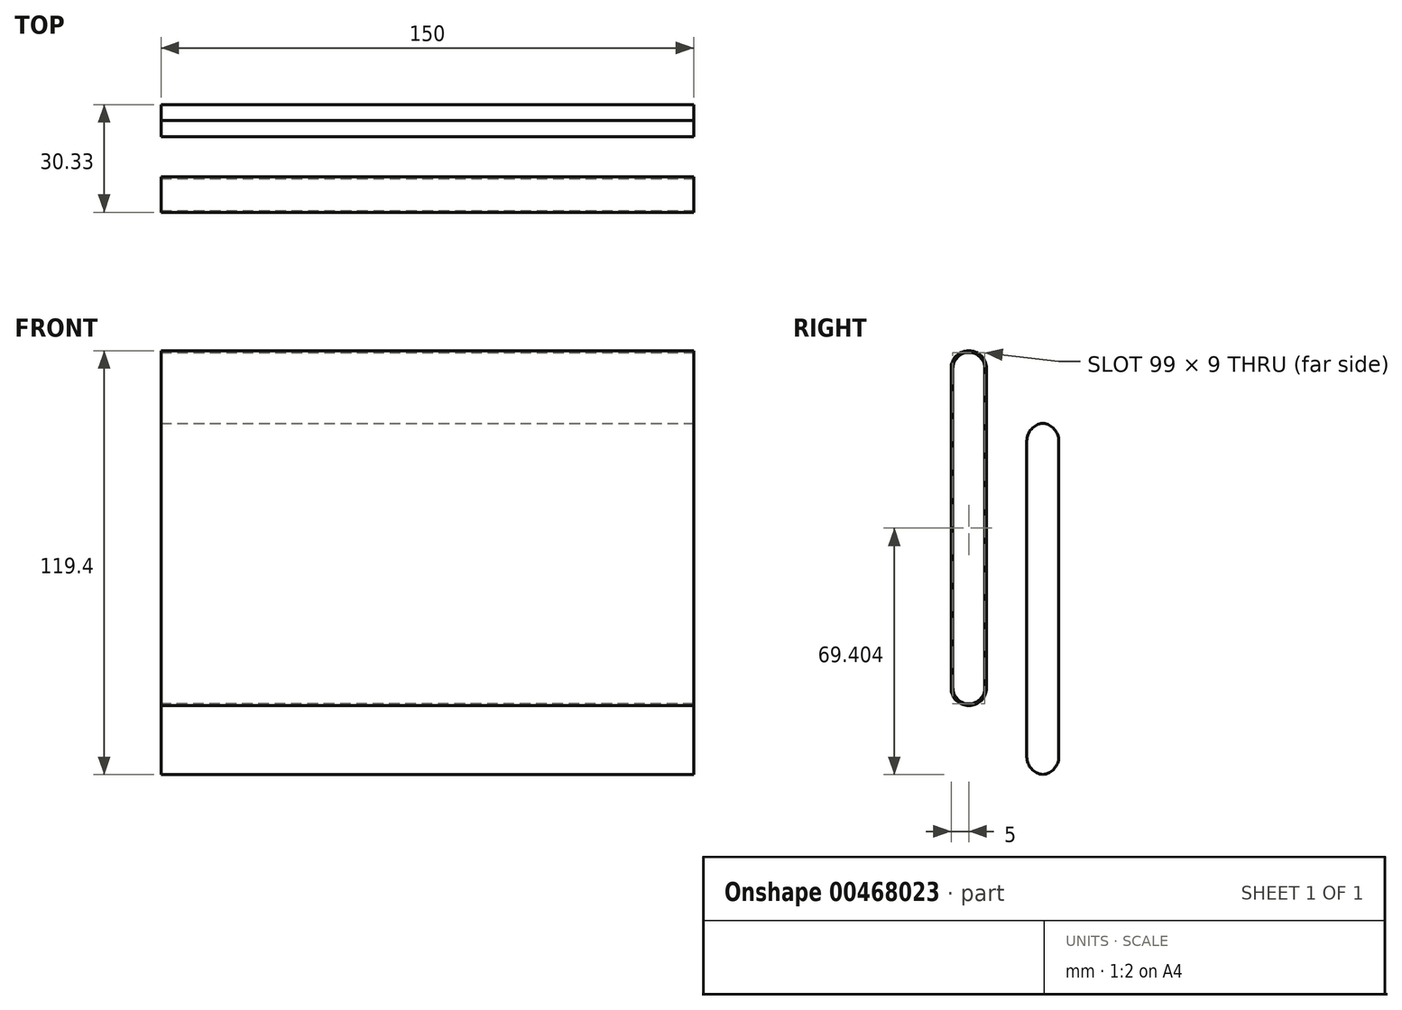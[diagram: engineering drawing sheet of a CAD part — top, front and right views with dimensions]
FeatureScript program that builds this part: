
annotation { "Feature Type Name" : "Feature", "Feature Type Description" : "" }
export const myFeature = defineFeature(function(context is Context, id is Id, definition is map)
    precondition{}
    {
        {
            var Q0;
            Q0=qCreatedBy(makeId("Front.planeOp"),FACE);
            var sketch = newSketch(context, id + "F0", { "sketchPlane" : qUnion([Q0])});
            skLineSegment(sketch, "E0.bottom", {"start": v(-64.3, 64.14) * mm, "end": v(85.7, 64.14) * mm});
            skLineSegment(sketch, "E0.top", {"start": v(-64.3, -35.86) * mm, "end": v(85.7, -35.86) * mm});
            skLineSegment(sketch, "E0.left", {"start": v(-64.3, 64.14) * mm, "end": v(-64.3, -35.86) * mm});
            skLineSegment(sketch, "E0.right", {"start": v(85.7, 64.14) * mm, "end": v(85.7, -35.86) * mm});
            skSolve(sketch);
        }
        {
            var Q0;
            Q0=makeQuery(id+"F0.imprint","IMPRINT",FACE,{"disambiguationData":[TD([[makeQuery(id+"F0.imprint","IMPRINT",EDGE,{"derivedFrom":sQuery(id+"F0.wireOp",EDGE,"E0.bottom")}),-1.0]])]});
            extrude(context, id + "F1", {"entities" : qUnion([Q0]), "depth" : 10 * mm});
        }
        {
            var Q0;
            Q0=makeQuery(id+"F1.opExtrude","CAP_EDGE",EDGE,{"disambiguationData":[OSD([sQuery(id+"F0.wireOp",EDGE,"E0.bottom")])],"isStart":false});
            var Q1;
            Q1=makeQuery(id+"F1.opExtrude","CAP_EDGE",EDGE,{"disambiguationData":[OSD([sQuery(id+"F0.wireOp",EDGE,"E0.bottom")])],"isStart":true});
            var Q2;
            Q2=makeQuery(id+"F1.opExtrude","CAP_EDGE",EDGE,{"disambiguationData":[OSD([sQuery(id+"F0.wireOp",EDGE,"E0.top")])],"isStart":false});
            var Q3;
            Q3=makeQuery(id+"F1.opExtrude","CAP_EDGE",EDGE,{"disambiguationData":[OSD([sQuery(id+"F0.wireOp",EDGE,"E0.top")])],"isStart":true});
            fillet(context, id + "F2", {"entities" : qUnion([Q0, Q1, Q2, Q3]), "radius" : 5 * mm, "tangentPropagation" : true, "allowEdgeOverflow" : false});
        }
        {
            var Q0;
            Q0=makeQuery(id+"F1.opExtrude","SWEPT_FACE",FACE,{"disambiguationData":[OSD([sQuery(id+"F0.wireOp",EDGE,"E0.right")])]});
            var Q1;
            Q1=makeQuery(id+"F1.opExtrude","SWEPT_FACE",FACE,{"disambiguationData":[OSD([sQuery(id+"F0.wireOp",EDGE,"E0.left")])]});
            shell(context, id + "F3", {"entities" : qUnion([Q0, Q1]), "thickness" : 0.5 * mm});
        }
        {
            var Q0;
            Q0=makeQuery(id+"F1.opExtrude","SWEPT_FACE",FACE,{"disambiguationData":[OSD([sQuery(id+"F0.wireOp",EDGE,"E0.right")])]});
            var sketch = newSketch(context, id + "F4", { "sketchPlane" : qUnion([Q0])});
            skLineSegment(sketch, "E1.bottom", {"start": v(20.33, 43.71) * mm, "end": v(11.33, 43.71) * mm});
            skLineSegment(sketch, "E1.top", {"start": v(20.33, -55.29) * mm, "end": v(11.33, -55.29) * mm});
            skLineSegment(sketch, "E1.left", {"start": v(20.33, 43.71) * mm, "end": v(20.33, -55.29) * mm});
            skLineSegment(sketch, "E1.right", {"start": v(11.33, 43.71) * mm, "end": v(11.33, -55.29) * mm});
            skSolve(sketch);
        }
        {
            var Q0;
            Q0=makeQuery(id+"F4.imprint","IMPRINT",FACE,{"disambiguationData":[TD([[makeQuery(id+"F4.imprint","IMPRINT",EDGE,{"derivedFrom":sQuery(id+"F4.wireOp",EDGE,"E1.bottom")}),1.0]])]});
            extrude(context, id + "F5", {"entities" : qUnion([Q0]), "oppositeDirection" : true, "depth" : 150 * mm});
        }
        {
            var Q0;
            Q0=makeQuery(id+"F5.opExtrude","SWEPT_EDGE",EDGE,{"disambiguationData":[OSD([sQuery(id+"F4.wireOp",EDGE,"E1.bottom"),sQuery(id+"F4.wireOp",EDGE,"E1.right")])]});
            var Q1;
            Q1=makeQuery(id+"F5.opExtrude","SWEPT_EDGE",EDGE,{"disambiguationData":[OSD([sQuery(id+"F4.wireOp",EDGE,"E1.bottom"),sQuery(id+"F4.wireOp",EDGE,"E1.left")])]});
            var Q2;
            Q2=makeQuery(id+"F5.opExtrude","SWEPT_EDGE",EDGE,{"disambiguationData":[OSD([sQuery(id+"F4.wireOp",EDGE,"E1.top"),sQuery(id+"F4.wireOp",EDGE,"E1.right")])]});
            var Q3;
            Q3=makeQuery(id+"F5.opExtrude","SWEPT_EDGE",EDGE,{"disambiguationData":[OSD([sQuery(id+"F4.wireOp",EDGE,"E1.top"),sQuery(id+"F4.wireOp",EDGE,"E1.left")])]});
            fillet(context, id + "F6", {"entities" : qUnion([Q0, Q1, Q2, Q3]), "radius" : 5 * mm, "tangentPropagation" : true, "allowEdgeOverflow" : false});
        }
    });
